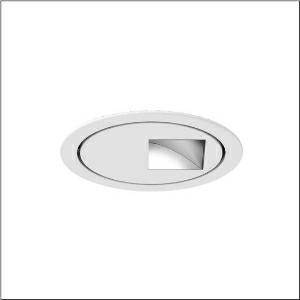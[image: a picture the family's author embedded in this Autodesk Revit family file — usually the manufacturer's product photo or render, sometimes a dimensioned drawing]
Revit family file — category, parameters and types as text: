
# Revit family: lunis_11_mini_round_51dk11cd2wf21
name_source: partatom
category: Lighting Fixtures
units: mm (PartAtom-declared; Revit-internal decimal feet)

## family parameters
Cut with Voids When Loaded = No
Host = Face
Light Source = No
Part Type = Normal
Room Calculation Point = No
Round Connector Dimension = Use Diameter
Shared = No

## types (1)
- Lunis 11 mini round (1 x LED 3000K / CRI = 80 (unbekannt), 2380 lm, 3000K)
    Apparent Load = 28 VA
    CIE Flux Codes = 44 77 97 100 100
    Color Rendering = 80
    Color Temperature = 3000K
    Default Elevation = 1800 mm
    Description = Lunis 11 mini round, downlight, light control with wallwasher, of highly reflective aluminium, highly specular, light emission: direct distribution, LED rated luminous flux: 2.380lm, light colour: 830, control gear: ECG, with terminal, 5-pole, mains connection: 220..230V, AC/DC, 0/50..60Hz, LED module, luminaire module, of aluminium, highly specular, white, diameter: 176mm, clamping range: 1..40mm, recessing ring, of plastic, traffic white (RAL 9016), protection rating (complete): IP20, insulation class (complete): insulation class II (safety insulation), certification: CE, permissible ambient temperature for indoor applications: 0..+35°C, packaging unit: 1 piece
    Height = 0 mm  [stored 0 ft]
    Lamp = 1 x LED 3000K / CRI >= 80 (unbekannt)
    Lamp Light Flux = 2380 lm
    Lamp count = 1
    Length = 176 mm
    Luminous efficacy = 86 lm/W
    Manufacturer = Siteco
    ModVariant = No
    Model = 51DK11CD2WF21
    Mounting Place = Ceiling
    Mounting Type = Recessed
    Number of Poles = 1
    OnlyDefault = Yes
    Power Factor = 1
    Product Name = Lunis 11 mini round
    Product group = downlight
    ProductGroupID = 400
    Protection Class = Protection class II
    Protection Degree = IP 20
    RLX_Detail_Level = 1
    RLX_Emergency_Light_Flux = 0 lm
    RLX_Emergency_Type = 0
    RLX_Emergency_Type_DB = No
    RlxData = <blob elided: 59353 chars, md5=2926a481>
    Socket = socket
    Standby Power = 0 W
    System Light Flux = 2380 lm
    System Power = 28 W
    Type Comments = Product without accessories
    Type Image = l_1004772.jpg
    URL = http://relux.com
    VarID = ---
    Voltage = 0 V
    Weight = 0.00 kg
    Width = 176 mm

note: [stored X ft] marks values corroborated as IEEE doubles in the binary element streams (Revit-internal decimal feet)

## geometry (parser evidence)
native form markers: Blend x4, Sweep x12
no freeform markers — native parametric forms only
